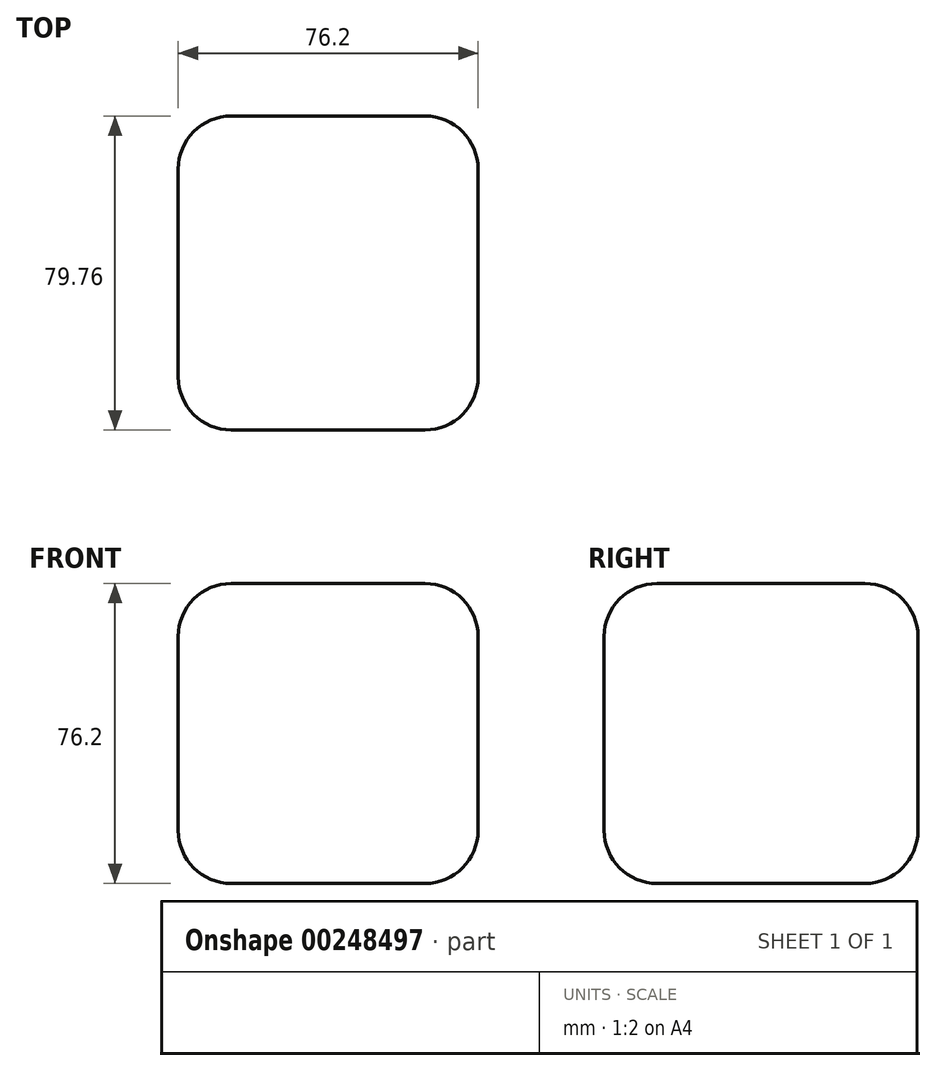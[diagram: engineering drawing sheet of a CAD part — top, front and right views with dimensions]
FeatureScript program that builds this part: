
annotation { "Feature Type Name" : "Feature", "Feature Type Description" : "" }
export const myFeature = defineFeature(function(context is Context, id is Id, definition is map)
    precondition{}
    {
        {
            var Q0;
            Q0=qCreatedBy(makeId("Front.planeOp"),FACE);
            var sketch = newSketch(context, id + "F0", { "sketchPlane" : qUnion([Q0])});
            skLineSegment(sketch, "E0.bottom", {"start": v(-38.43, 41.03) * mm, "end": v(37.77, 41.03) * mm});
            skLineSegment(sketch, "E0.top", {"start": v(-38.43, -35.17) * mm, "end": v(37.77, -35.17) * mm});
            skLineSegment(sketch, "E0.left", {"start": v(-38.43, 41.03) * mm, "end": v(-38.43, -35.17) * mm});
            skLineSegment(sketch, "E0.right", {"start": v(37.77, 41.03) * mm, "end": v(37.77, -35.17) * mm});
            skSolve(sketch);
        }
        {
            var Q0;
            Q0=makeQuery(id+"F0.imprint","IMPRINT",FACE,{"disambiguationData":[TD([[makeQuery(id+"F0.imprint","IMPRINT",EDGE,{"derivedFrom":sQuery(id+"F0.wireOp",EDGE,"E0.bottom")}),-1.0]])]});
            extrude(context, id + "F1", {"entities" : qUnion([Q0]), "depth" : 79.76 * mm});
        }
        {
            var Q0;
            Q0=makeQuery(id+"F1.opExtrude","SWEPT_EDGE",EDGE,{"disambiguationData":[OSD([sQuery(id+"F0.wireOp",EDGE,"E0.bottom"),sQuery(id+"F0.wireOp",EDGE,"E0.left")])]});
            var Q1;
            Q1=makeQuery(id+"F1.opExtrude","SWEPT_EDGE",EDGE,{"disambiguationData":[OSD([sQuery(id+"F0.wireOp",EDGE,"E0.bottom"),sQuery(id+"F0.wireOp",EDGE,"E0.right")])]});
            var Q2;
            Q2=makeQuery(id+"F1.opExtrude","CAP_EDGE",EDGE,{"disambiguationData":[OSD([sQuery(id+"F0.wireOp",EDGE,"E0.bottom")])],"isStart":false});
            var Q3;
            Q3=makeQuery(id+"F1.opExtrude","SWEPT_FACE",FACE,{"disambiguationData":[OSD([sQuery(id+"F0.wireOp",EDGE,"E0.bottom")])]});
            var Q4;
            Q4=makeQuery(id+"F1.opExtrude","CAP_EDGE",EDGE,{"disambiguationData":[OSD([sQuery(id+"F0.wireOp",EDGE,"E0.left")])],"isStart":false});
            var Q5;
            Q5=makeQuery(id+"F1.opExtrude","CAP_EDGE",EDGE,{"disambiguationData":[OSD([sQuery(id+"F0.wireOp",EDGE,"E0.left")])],"isStart":true});
            var Q6;
            Q6=makeQuery(id+"F1.opExtrude","SWEPT_EDGE",EDGE,{"disambiguationData":[OSD([sQuery(id+"F0.wireOp",EDGE,"E0.top"),sQuery(id+"F0.wireOp",EDGE,"E0.left")])]});
            var Q7;
            Q7=makeQuery(id+"F1.opExtrude","CAP_EDGE",EDGE,{"disambiguationData":[OSD([sQuery(id+"F0.wireOp",EDGE,"E0.top")])],"isStart":false});
            var Q8;
            Q8=makeQuery(id+"F1.opExtrude","CAP_EDGE",EDGE,{"disambiguationData":[OSD([sQuery(id+"F0.wireOp",EDGE,"E0.right")])],"isStart":false});
            var Q9;
            Q9=makeQuery(id+"F1.opExtrude","CAP_EDGE",EDGE,{"disambiguationData":[OSD([sQuery(id+"F0.wireOp",EDGE,"E0.right")])],"isStart":true});
            var Q10;
            Q10=makeQuery(id+"F1.opExtrude","CAP_EDGE",EDGE,{"disambiguationData":[OSD([sQuery(id+"F0.wireOp",EDGE,"E0.top")])],"isStart":true});
            var Q11;
            Q11=makeQuery(id+"F1.opExtrude","SWEPT_EDGE",EDGE,{"disambiguationData":[OSD([sQuery(id+"F0.wireOp",EDGE,"E0.top"),sQuery(id+"F0.wireOp",EDGE,"E0.right")])]});
            fillet(context, id + "F2", {"entities" : qUnion([Q0, Q1, Q2, Q3, Q4, Q5, Q6, Q7, Q8, Q9, Q10, Q11]), "radius" : 13.5 * mm, "tangentPropagation" : true, "allowEdgeOverflow" : false});
        }
    });
